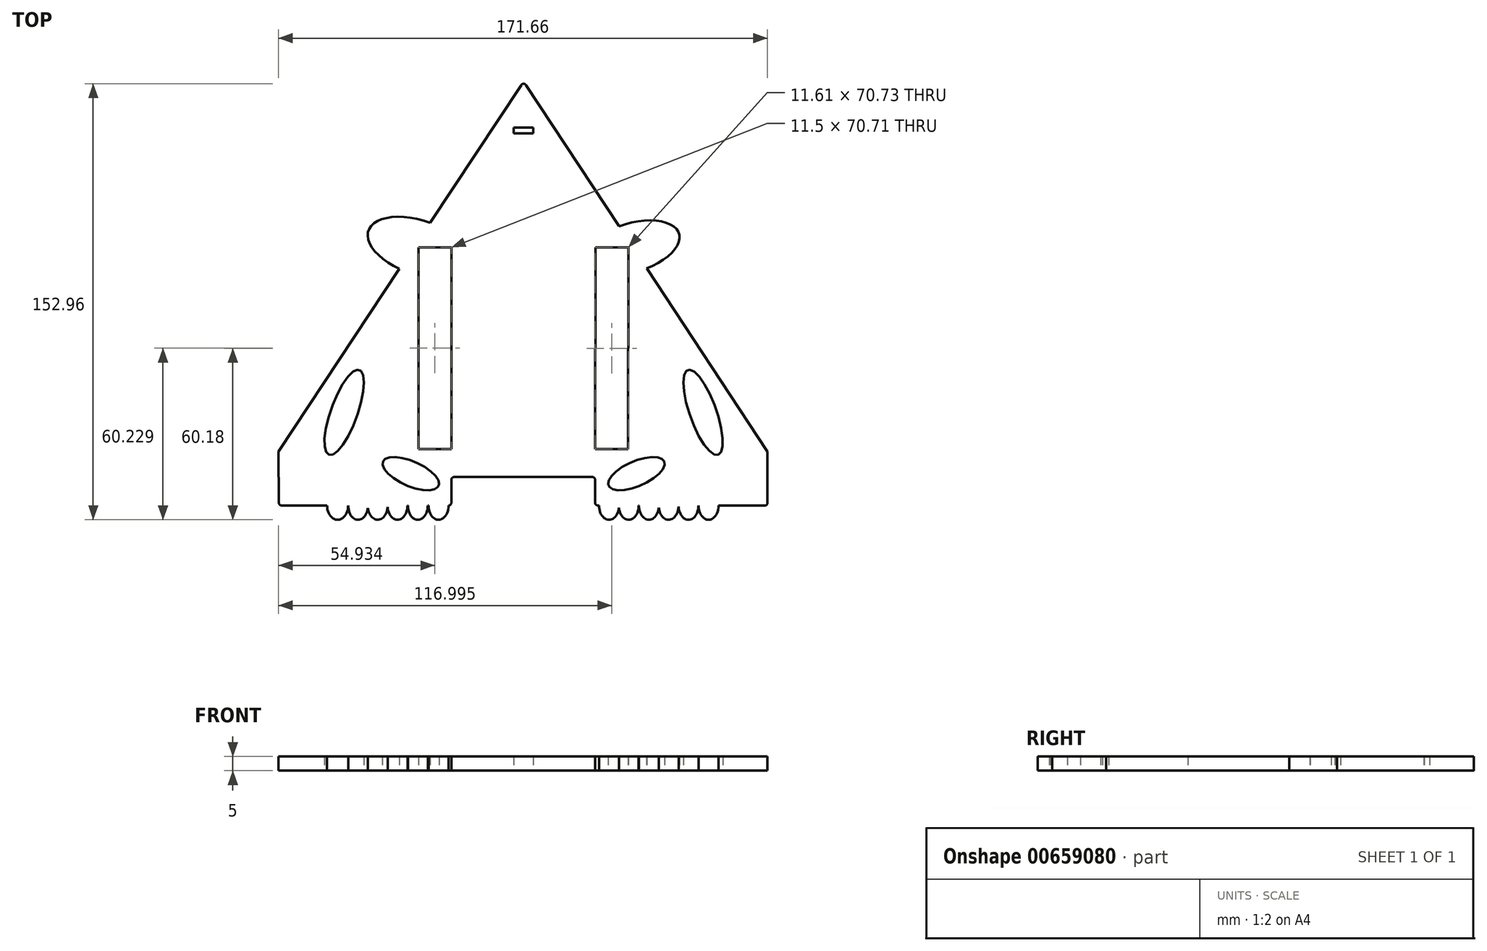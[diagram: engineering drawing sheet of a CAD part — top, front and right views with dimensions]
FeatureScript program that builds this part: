
annotation { "Feature Type Name" : "Feature", "Feature Type Description" : "" }
export const myFeature = defineFeature(function(context is Context, id is Id, definition is map)
    precondition{}
    {
        {
            var Q0;
            Q0=qCreatedBy(makeId("Top.planeOp"),FACE);
            var sketch = newSketch(context, id + "F0", { "sketchPlane" : qUnion([Q0])});
            skPoint(sketch, "E0.0.midPoint", {"position": v(0, -49.5) * mm});
            skPoint(sketch, "E0.cCircle.center.orphan", {"position": v(0, 0) * mm});
            skLineSegment(sketch, "E1", {"start": v(-84.75, -49.5) * mm, "end": v(-54.5, -49.5) * mm});
            skLineSegment(sketch, "E2", {"start": v(84.74, -49.5) * mm, "end": v(26.24, -49.5) * mm});
            skLineSegment(sketch, "E3", {"start": v(25.24, -48.5) * mm, "end": v(25.24, -40.5) * mm});
            skLineSegment(sketch, "E4", {"start": v(24.24, -39.5) * mm, "end": v(-24.24, -39.5) * mm});
            skLineSegment(sketch, "E5", {"start": v(-25.24, -40.5) * mm, "end": v(-25.24, -48.5) * mm});
            skPoint(sketch, "E6.visualSharp", {"position": v(0.12, 99.27) * mm});
            skLineSegment(sketch, "E7", {"start": v(0.95, 98) * mm, "end": v(33.6, 48.5) * mm});
            skLineSegment(sketch, "E8", {"start": v(85.74, -30.56) * mm, "end": v(85.74, -48.5) * mm});
            skLineSegment(sketch, "E9", {"start": v(-85.92, -30.56) * mm, "end": v(-85.75, -48.5) * mm});
            skLineSegment(sketch, "E10", {"start": v(-0.72, 98.01) * mm, "end": v(-33.53, 48.5) * mm});
            skArc(sketch, "E11.filletArc", {"start": v(0.95, 98) * mm, "mid": v(0.12, 98.46) * mm, "end": v(-0.72, 98.01) * mm});
            skPoint(sketch, "E12.visualSharp", {"position": v(85.74, -49.5) * mm});
            skArc(sketch, "E12.filletArc", {"start": v(84.74, -49.5) * mm, "mid": v(85.44, -49.2) * mm, "end": v(85.74, -48.5) * mm});
            skPoint(sketch, "E13.visualSharp", {"position": v(25.24, -49.5) * mm});
            skArc(sketch, "E13.filletArc", {"start": v(25.24, -48.5) * mm, "mid": v(25.53, -49.2) * mm, "end": v(26.24, -49.5) * mm});
            skPoint(sketch, "E14.visualSharp", {"position": v(-85.74, -49.5) * mm});
            skArc(sketch, "E14.filletArc", {"start": v(-85.75, -48.5) * mm, "mid": v(-85.45, -49.21) * mm, "end": v(-84.75, -49.5) * mm});
            skPoint(sketch, "E15.visualSharp", {"position": v(-25.24, -49.5) * mm});
            skArc(sketch, "E15.filletArc", {"start": v(-26.24, -49.5) * mm, "mid": v(-25.53, -49.2) * mm, "end": v(-25.24, -48.5) * mm});
            skPoint(sketch, "E16.visualSharp", {"position": v(25.24, -39.5) * mm});
            skArc(sketch, "E16.filletArc", {"start": v(25.24, -40.5) * mm, "mid": v(24.94, -39.8) * mm, "end": v(24.24, -39.5) * mm});
            skPoint(sketch, "E17.visualSharp", {"position": v(-25.24, -39.5) * mm});
            skArc(sketch, "E17.filletArc", {"start": v(-24.24, -39.5) * mm, "mid": v(-24.94, -39.8) * mm, "end": v(-25.24, -40.5) * mm});
            skEllipticalArc(sketch, "E18", {});
            skEllipticalArc(sketch, "E19", {});
            skEllipticalArc(sketch, "E20", {});
            skEllipticalArc(sketch, "E21", {});
            skEllipticalArc(sketch, "E22", {});
            skEllipticalArc(sketch, "E23", {});
            skPoint(sketch, "E24", {"position": v(-54.44, -49.5) * mm});
            skPoint(sketch, "E25", {"position": v(-54.56, -49.5) * mm});
            skPoint(sketch, "E26", {"position": v(-54.49, -50.37) * mm});
            skLineSegment(sketch, "E27", {"start": v(-54.5, -49.5) * mm, "end": v(-54.5, -50.43) * mm});
            skPoint(sketch, "E28", {"position": v(-47.57, -49.95) * mm});
            skLineSegment(sketch, "E29", {"start": v(-47.58, -50.05) * mm, "end": v(-47.58, -49.5) * mm});
            skLineSegment(sketch, "E30.trimOffspring", {"start": v(-54.44, -49.5) * mm, "end": v(-26.24, -49.5) * mm});
            skEllipticalArc(sketch, "E31", {});
            skEllipticalArc(sketch, "E32", {});
            skEllipticalArc(sketch, "E33", {});
            skEllipticalArc(sketch, "E34", {});
            skEllipticalArc(sketch, "E35", {});
            skEllipticalArc(sketch, "E36", {});
            skPoint(sketch, "E37", {"position": v(26.6, -49.5) * mm});
            skPoint(sketch, "E38", {"position": v(33.53, -49.5) * mm});
            skPoint(sketch, "E39", {"position": v(40.6, -49.5) * mm});
            skPoint(sketch, "E40", {"position": v(40.53, -49.5) * mm});
            skPoint(sketch, "E41", {"position": v(47.6, -49.5) * mm});
            skPoint(sketch, "E42", {"position": v(47.52, -49.5) * mm});
            skPoint(sketch, "E43", {"position": v(54.52, -49.5) * mm});
            skPoint(sketch, "E44", {"position": v(54.5, -49.5) * mm});
            skPoint(sketch, "E45", {"position": v(61.53, -49.5) * mm});
            skPoint(sketch, "E46", {"position": v(61.5, -49.5) * mm});
            skPoint(sketch, "E47", {"position": v(68.53, -49.5) * mm});
            skPoint(sketch, "E48", {"position": v(33.6, -49.5) * mm});
            skLineSegment(sketch, "E49.trimOffspring", {"start": v(-43.32, 33.72) * mm, "end": v(-85.92, -30.56) * mm});
            skEllipticalArc(sketch, "E50", {});
            skLineSegment(sketch, "E51.trimOffspring", {"start": v(43.34, 33.72) * mm, "end": v(85.74, -30.56) * mm});
            skEllipticalArc(sketch, "E52", {});
            skPoint(sketch, "E53", {"position": v(-33.53, 48.5) * mm});
            skPoint(sketch, "E54", {"position": v(-43.32, 33.72) * mm});
            skLineSegment(sketch, "E55", {"start": v(-33.53, 48.5) * mm, "end": v(-31.35, 49.17) * mm});
            skLineSegment(sketch, "E56", {"start": v(33.6, 48.5) * mm, "end": v(33.66, 48.45) * mm});
            skEllipse(sketch, "E57", {"center": v(63.09, -16.83) * mm, "majorRadius": 15.8 * mm, "minorRadius": 4.7 * mm, "majorAxis": v(0.34, -0.94)});
            skEllipse(sketch, "E58", {"center": v(39.7, -38.3) * mm, "majorRadius": 10.66 * mm, "minorRadius": 4.36 * mm, "majorAxis": v(0.92, 0.4)});
            skEllipse(sketch, "E59.MirrorC", {"center": v(-62.85, -16.83) * mm, "majorRadius": 15.8 * mm, "minorRadius": 4.7 * mm, "majorAxis": v(-0.34, -0.94)});
            skEllipse(sketch, "E60.MirrorC", {"center": v(-39.47, -38.3) * mm, "majorRadius": 10.66 * mm, "minorRadius": 4.36 * mm, "majorAxis": v(-0.92, 0.4)});
            skLineSegment(sketch, "E61.trimOffspring", {"start": v(43.32, 33.72) * mm, "end": v(43.34, 33.72) * mm});
            skLineSegment(sketch, "E62", {"start": v(-36.74, 41.09) * mm, "end": v(-36.74, -29.63) * mm});
            skLineSegment(sketch, "E63", {"start": v(-36.74, 41.09) * mm, "end": v(-25.24, 41.09) * mm});
            skLineSegment(sketch, "E64", {"start": v(-36.74, -29.63) * mm, "end": v(-25.24, -29.63) * mm});
            skLineSegment(sketch, "E65", {"start": v(-25.24, -29.63) * mm, "end": v(-25.24, 41.09) * mm});
            skLineSegment(sketch, "E66.MirrorCS", {"start": v(25.27, -29.67) * mm, "end": v(25.38, 41.05) * mm});
            skLineSegment(sketch, "E67.MirrorCS", {"start": v(36.88, 41.03) * mm, "end": v(36.77, -29.69) * mm});
            skLineSegment(sketch, "E68.MirrorCS", {"start": v(36.88, 41.03) * mm, "end": v(25.38, 41.05) * mm});
            skLineSegment(sketch, "E69.MirrorCS", {"start": v(36.77, -29.69) * mm, "end": v(25.27, -29.67) * mm});
            skLineSegment(sketch, "E70", {"start": v(-3.33, 83.04) * mm, "end": v(0, 83.04) * mm});
            skLineSegment(sketch, "E71", {"start": v(-3.33, 83.04) * mm, "end": v(-3.33, 81.04) * mm});
            skLineSegment(sketch, "E72", {"start": v(-3.33, 81.04) * mm, "end": v(0, 81.04) * mm});
            skLineSegment(sketch, "E73.MirrorCS", {"start": v(3.54, 83.04) * mm, "end": v(0.21, 83.04) * mm});
            skLineSegment(sketch, "E74.MirrorCS", {"start": v(3.54, 81.04) * mm, "end": v(0.2, 81.04) * mm});
            skLineSegment(sketch, "E75.MirrorCS", {"start": v(3.54, 83.04) * mm, "end": v(3.54, 81.04) * mm});
            skLineSegment(sketch, "E76", {"start": v(0, 81.04) * mm, "end": v(0.2, 81.04) * mm});
            skLineSegment(sketch, "E77", {"start": v(0, 83.04) * mm, "end": v(0.21, 83.04) * mm});
            const initialGuessF0  = {"E18": [-0.029729247093200684, -0.0495000034570694, 0, -1, 0.005, 0.0035, 4.71238898038469, 1.570801617782231], "E19": [-0.03698873519897461, -0.0495000034570694, 0, -1, 0.005, 0.0035, 4.71238898038469, 1.5707963267948966], "E20": [-0.044100072234869, -0.0495000034570694, 0, -1, 0.005, 0.0035, 4.822721470064113, 1.5707963267948966], "E21": [-0.05105750903492189, -0.0495000034570694, 0, -1, 0.005, 0.0035, 4.899477820012888, 1.4604638371154721], "E22": [-0.05793535813684248, -0.0495000034570694, 0, -1, 0.005, 0.0035, 4.71238898038469, 1.3953355132787328], "E23": [-0.06513869762420654, -0.0495000034570694, 0, -1, 0.005, 0.0037033394873640557, 4.71238898038469, 1.5707963267948966], "E31": [0.030106185004115105, -0.04950000345706941, 0, -1, 0.005, 0.0035, 4.71238898038469, 1.5707963267948966], "E32": [0.037028003484010696, -0.04950000345706941, 0, -1, 0.005, 0.0035, 4.71238898038469, 1.5707963267948966], "E33": [0.044100940227508545, -0.04950000345706941, 0, -1, 0.005, 0.0035, 4.71238898038469, 1.5707963267948966], "E34": [0.05102432146668434, -0.04950000345706941, 0, -1, 0.005, 0.0035, 4.71238898038469, 1.5707963267948966], "E35": [0.05800028517842293, -0.04950000345706941, 0, -1, 0.005, 0.0035, 4.71238898038469, 1.5707963267948966], "E36": [0.06503187119960785, -0.04950000345706941, 0, -1, 0.005, 0.0035, 4.71238898038469, 1.5707963267948966], "E50": [-0.03673652096247923, 0.04108645766973406, 0.9491522126047598, -0.31481753017817954, 0.018534346020662177, 0.009462294803832105, 1.4319341267225272, 4.495986690844154], "E52": [0.03848833608708242, 0.041086457669728384, -0.9600526165022497, -0.2798195374651036, 0.016875, 0.008521082131865629, 1.7240567735104766, 4.865276969991962]};
            skSetInitialGuess(sketch, initialGuessF0);
            skSolve(sketch);
        }
        {
            var Q0;
            Q0 = qSketchRegion(id + "F0", true);
            var Q1;
            Q1 = qSketchRegion(id + "FPg5yT2tUSxsPf8_0", true);
            extrude(context, id + "F1", {"entities" : qUnion([Q0, Q1]), "depth" : 5 * mm, "offsetDistance" : 25 * mm});
        }
    });
